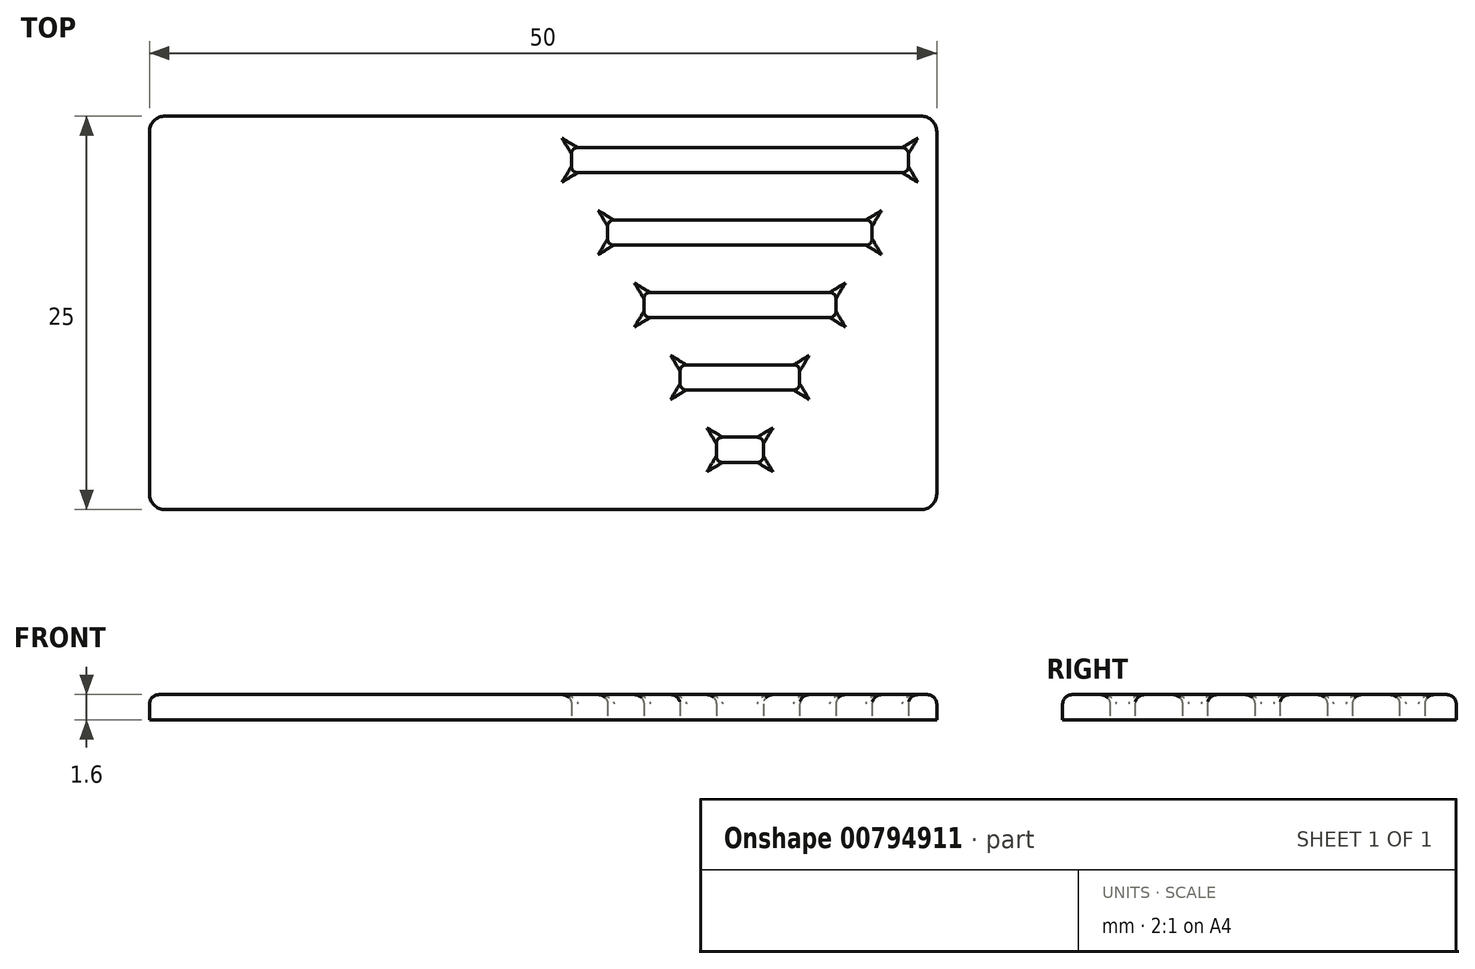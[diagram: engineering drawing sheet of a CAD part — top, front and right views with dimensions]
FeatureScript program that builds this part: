
annotation { "Feature Type Name" : "Feature", "Feature Type Description" : "" }
export const myFeature = defineFeature(function(context is Context, id is Id, definition is map)
    precondition{}
    {
        {
            var Q0;
            Q0=qCreatedBy(makeId("Top.planeOp"),FACE);
            var sketch = newSketch(context, id + "F0", { "sketchPlane" : qUnion([Q0])});
            skLineSegment(sketch, "E0.bottom", {"start": v(-25, 12.5) * mm, "end": v(25, 12.5) * mm});
            skLineSegment(sketch, "E0.top", {"start": v(-25, -12.5) * mm, "end": v(25, -12.5) * mm});
            skLineSegment(sketch, "E0.left", {"start": v(-25, 12.5) * mm, "end": v(-25, -12.5) * mm});
            skLineSegment(sketch, "E0.right", {"start": v(25, 12.5) * mm, "end": v(25, -12.5) * mm});
            skLineSegment(sketch, "E1", {"start": v(-25, 12.5) * mm, "end": v(25, -12.5) * mm, "construction": true});
            skLineSegment(sketch, "E2", {"start": v(0, 12.5) * mm, "end": v(0, -12.5) * mm, "construction": true});
            skLineSegment(sketch, "E3", {"start": v(0, 12.5) * mm, "end": v(12.5, -12.5) * mm, "construction": true});
            skLineSegment(sketch, "E4", {"start": v(12.5, -12.5) * mm, "end": v(25, 12.5) * mm, "construction": true});
            skLineSegment(sketch, "E5.bottom", {"start": v(11, -9.5) * mm, "end": v(14, -9.5) * mm});
            skLineSegment(sketch, "E5.top", {"start": v(11, -7.9) * mm, "end": v(14, -7.9) * mm});
            skLineSegment(sketch, "E5.left", {"start": v(11, -9.5) * mm, "end": v(11, -7.9) * mm});
            skLineSegment(sketch, "E5.right", {"start": v(14, -9.5) * mm, "end": v(14, -7.9) * mm});
            skLineSegment(sketch, "E6.bottom", {"start": v(6.4, -0.3) * mm, "end": v(18.6, -0.3) * mm});
            skLineSegment(sketch, "E6.top", {"start": v(6.4, 1.3) * mm, "end": v(18.6, 1.3) * mm});
            skLineSegment(sketch, "E6.left", {"start": v(6.4, -0.3) * mm, "end": v(6.4, 1.3) * mm});
            skLineSegment(sketch, "E6.right", {"start": v(18.6, -0.3) * mm, "end": v(18.6, 1.3) * mm});
            skLineSegment(sketch, "E7.bottom", {"start": v(8.7, -4.9) * mm, "end": v(16.3, -4.9) * mm});
            skLineSegment(sketch, "E7.top", {"start": v(8.7, -3.3) * mm, "end": v(16.3, -3.3) * mm});
            skLineSegment(sketch, "E7.left", {"start": v(8.7, -4.9) * mm, "end": v(8.7, -3.3) * mm});
            skLineSegment(sketch, "E7.right", {"start": v(16.3, -4.9) * mm, "end": v(16.3, -3.3) * mm});
            skLineSegment(sketch, "E8", {"start": v(11, -12.5) * mm, "end": v(11, -9.5) * mm, "construction": true});
            skLineSegment(sketch, "E9", {"start": v(11, -7.9) * mm, "end": v(11, -4.9) * mm, "construction": true});
            skLineSegment(sketch, "E10", {"start": v(8.7, -3.3) * mm, "end": v(8.7, -0.3) * mm, "construction": true});
            skLineSegment(sketch, "E11.bottom", {"start": v(4.1, 4.3) * mm, "end": v(20.9, 4.3) * mm});
            skLineSegment(sketch, "E11.top", {"start": v(4.1, 5.9) * mm, "end": v(20.9, 5.9) * mm});
            skLineSegment(sketch, "E11.left", {"start": v(4.1, 4.3) * mm, "end": v(4.1, 5.9) * mm});
            skLineSegment(sketch, "E11.right", {"start": v(20.9, 4.3) * mm, "end": v(20.9, 5.9) * mm});
            skLineSegment(sketch, "E12", {"start": v(6.4, 1.3) * mm, "end": v(6.4, 4.3) * mm, "construction": true});
            skLineSegment(sketch, "E13.bottom", {"start": v(1.8, 8.9) * mm, "end": v(23.2, 8.9) * mm});
            skLineSegment(sketch, "E13.top", {"start": v(1.8, 10.5) * mm, "end": v(23.2, 10.5) * mm});
            skLineSegment(sketch, "E13.left", {"start": v(1.8, 8.9) * mm, "end": v(1.8, 10.5) * mm});
            skLineSegment(sketch, "E13.right", {"start": v(23.2, 8.9) * mm, "end": v(23.2, 10.5) * mm});
            skLineSegment(sketch, "E14", {"start": v(4.1, 5.9) * mm, "end": v(4.1, 8.9) * mm, "construction": true});
            skLineSegment(sketch, "E15", {"start": v(4.1, 10.5) * mm, "end": v(4.1, 12.5) * mm, "construction": true});
            skSolve(sketch);
        }
        {
            var Q0;
            Q0=makeQuery(id+"F0.imprint","IMPRINT",FACE,{"disambiguationData":[TD([[makeQuery(id+"F0.imprint","IMPRINT",EDGE,{"derivedFrom":sQuery(id+"F0.wireOp",EDGE,"E0.bottom")}),-1.0]])]});
            extrude(context, id + "F1", {"entities" : qUnion([Q0]), "depth" : 1.6 * mm, "offsetDistance" : 25 * mm});
        }
        {
            var Q0;
            Q0=makeQuery(id+"F1.opExtrude","CAP_FACE",FACE,{"disambiguationData":[OSD([sQuery(id+"F0.wireOp",EDGE,"E0.bottom"),sQuery(id+"F0.wireOp",EDGE,"E0.top"),sQuery(id+"F0.wireOp",EDGE,"E0.left"),sQuery(id+"F0.wireOp",EDGE,"E0.right"),sQuery(id+"F0.wireOp",EDGE,"E5.bottom"),sQuery(id+"F0.wireOp",EDGE,"E5.top"),sQuery(id+"F0.wireOp",EDGE,"E5.left"),sQuery(id+"F0.wireOp",EDGE,"E5.right"),sQuery(id+"F0.wireOp",EDGE,"E6.bottom"),sQuery(id+"F0.wireOp",EDGE,"E6.top"),sQuery(id+"F0.wireOp",EDGE,"E6.left"),sQuery(id+"F0.wireOp",EDGE,"E6.right"),sQuery(id+"F0.wireOp",EDGE,"E7.bottom"),sQuery(id+"F0.wireOp",EDGE,"E7.top"),sQuery(id+"F0.wireOp",EDGE,"E7.left"),sQuery(id+"F0.wireOp",EDGE,"E7.right"),sQuery(id+"F0.wireOp",EDGE,"E11.bottom"),sQuery(id+"F0.wireOp",EDGE,"E11.top"),sQuery(id+"F0.wireOp",EDGE,"E11.left"),sQuery(id+"F0.wireOp",EDGE,"E11.right"),sQuery(id+"F0.wireOp",EDGE,"E13.bottom"),sQuery(id+"F0.wireOp",EDGE,"E13.top"),sQuery(id+"F0.wireOp",EDGE,"E13.left"),sQuery(id+"F0.wireOp",EDGE,"E13.right")])],"isStart":false});
            fillet(context, id + "F2", {"entities" : qUnion([Q0]), "radius" : 0.6 * mm, "tangentPropagation" : true, "allowEdgeOverflow" : false});
        }
        {
            var Q0;
            Q0=makeQuery(id+"F1.opExtrude","SWEPT_EDGE",EDGE,{"disambiguationData":[OSD([sQuery(id+"F0.wireOp",EDGE,"E11.bottom"),sQuery(id+"F0.wireOp",EDGE,"E11.right")])]});
            var Q1;
            Q1=makeQuery(id+"F1.opExtrude","SWEPT_EDGE",EDGE,{"disambiguationData":[OSD([sQuery(id+"F0.wireOp",EDGE,"E6.bottom"),sQuery(id+"F0.wireOp",EDGE,"E6.right")])]});
            var Q2;
            Q2=makeQuery(id+"F1.opExtrude","SWEPT_EDGE",EDGE,{"disambiguationData":[OSD([sQuery(id+"F0.wireOp",EDGE,"E7.bottom"),sQuery(id+"F0.wireOp",EDGE,"E7.right")])]});
            var Q3;
            Q3=makeQuery(id+"F1.opExtrude","SWEPT_EDGE",EDGE,{"disambiguationData":[OSD([sQuery(id+"F0.wireOp",EDGE,"E5.bottom"),sQuery(id+"F0.wireOp",EDGE,"E5.right")])]});
            var Q4;
            Q4=makeQuery(id+"F1.opExtrude","SWEPT_EDGE",EDGE,{"disambiguationData":[OSD([sQuery(id+"F0.wireOp",EDGE,"E7.top"),sQuery(id+"F0.wireOp",EDGE,"E7.right")])]});
            var Q5;
            Q5=makeQuery(id+"F1.opExtrude","SWEPT_EDGE",EDGE,{"disambiguationData":[OSD([sQuery(id+"F0.wireOp",EDGE,"E6.top"),sQuery(id+"F0.wireOp",EDGE,"E6.right")])]});
            var Q6;
            Q6=makeQuery(id+"F1.opExtrude","SWEPT_EDGE",EDGE,{"disambiguationData":[OSD([sQuery(id+"F0.wireOp",EDGE,"E11.top"),sQuery(id+"F0.wireOp",EDGE,"E11.right")])]});
            var Q7;
            Q7=makeQuery(id+"F1.opExtrude","SWEPT_EDGE",EDGE,{"disambiguationData":[OSD([sQuery(id+"F0.wireOp",EDGE,"E13.top"),sQuery(id+"F0.wireOp",EDGE,"E13.right")])]});
            var Q8;
            Q8=makeQuery(id+"F1.opExtrude","SWEPT_EDGE",EDGE,{"disambiguationData":[OSD([sQuery(id+"F0.wireOp",EDGE,"E5.top"),sQuery(id+"F0.wireOp",EDGE,"E5.right")])]});
            var Q9;
            Q9=makeQuery(id+"F1.opExtrude","SWEPT_EDGE",EDGE,{"disambiguationData":[OSD([sQuery(id+"F0.wireOp",EDGE,"E13.top"),sQuery(id+"F0.wireOp",EDGE,"E13.left")])]});
            var Q10;
            Q10=makeQuery(id+"F1.opExtrude","SWEPT_EDGE",EDGE,{"disambiguationData":[OSD([sQuery(id+"F0.wireOp",EDGE,"E11.top"),sQuery(id+"F0.wireOp",EDGE,"E11.left")])]});
            var Q11;
            Q11=makeQuery(id+"F1.opExtrude","SWEPT_EDGE",EDGE,{"disambiguationData":[OSD([sQuery(id+"F0.wireOp",EDGE,"E6.top"),sQuery(id+"F0.wireOp",EDGE,"E6.left")])]});
            var Q12;
            Q12=makeQuery(id+"F1.opExtrude","SWEPT_EDGE",EDGE,{"disambiguationData":[OSD([sQuery(id+"F0.wireOp",EDGE,"E7.top"),sQuery(id+"F0.wireOp",EDGE,"E7.left")])]});
            var Q13;
            Q13=makeQuery(id+"F1.opExtrude","SWEPT_EDGE",EDGE,{"disambiguationData":[OSD([sQuery(id+"F0.wireOp",EDGE,"E5.top"),sQuery(id+"F0.wireOp",EDGE,"E5.left")])]});
            var Q14;
            Q14=makeQuery(id+"F1.opExtrude","SWEPT_EDGE",EDGE,{"disambiguationData":[OSD([sQuery(id+"F0.wireOp",EDGE,"E7.bottom"),sQuery(id+"F0.wireOp",EDGE,"E7.left")])]});
            var Q15;
            Q15=makeQuery(id+"F1.opExtrude","SWEPT_EDGE",EDGE,{"disambiguationData":[OSD([sQuery(id+"F0.wireOp",EDGE,"E6.bottom"),sQuery(id+"F0.wireOp",EDGE,"E6.left")])]});
            var Q16;
            Q16=makeQuery(id+"F1.opExtrude","SWEPT_EDGE",EDGE,{"disambiguationData":[OSD([sQuery(id+"F0.wireOp",EDGE,"E11.bottom"),sQuery(id+"F0.wireOp",EDGE,"E11.left")])]});
            var Q17;
            Q17=makeQuery(id+"F1.opExtrude","SWEPT_EDGE",EDGE,{"disambiguationData":[OSD([sQuery(id+"F0.wireOp",EDGE,"E13.bottom"),sQuery(id+"F0.wireOp",EDGE,"E13.left")])]});
            var Q18;
            Q18=makeQuery(id+"F1.opExtrude","SWEPT_EDGE",EDGE,{"disambiguationData":[OSD([sQuery(id+"F0.wireOp",EDGE,"E5.bottom"),sQuery(id+"F0.wireOp",EDGE,"E5.left")])]});
            var Q19;
            Q19=makeQuery(id+"F1.opExtrude","SWEPT_EDGE",EDGE,{"disambiguationData":[OSD([sQuery(id+"F0.wireOp",EDGE,"E13.bottom"),sQuery(id+"F0.wireOp",EDGE,"E13.right")])]});
            fillet(context, id + "F3", {"entities" : qUnion([Q0, Q1, Q2, Q3, Q4, Q5, Q6, Q7, Q8, Q9, Q10, Q11, Q12, Q13, Q14, Q15, Q16, Q17, Q18, Q19]), "radius" : 0.4 * mm, "tangentPropagation" : true, "allowEdgeOverflow" : false});
        }
        {
            var Q0;
            Q0=makeQuery(id+"F1.opExtrude","SWEPT_EDGE",EDGE,{"disambiguationData":[OSD([sQuery(id+"F0.wireOp",EDGE,"E0.bottom"),sQuery(id+"F0.wireOp",EDGE,"E0.right")])]});
            var Q1;
            Q1=makeQuery(id+"F1.opExtrude","SWEPT_EDGE",EDGE,{"disambiguationData":[OSD([sQuery(id+"F0.wireOp",EDGE,"E0.top"),sQuery(id+"F0.wireOp",EDGE,"E0.right")])]});
            var Q2;
            Q2=makeQuery(id+"F1.opExtrude","SWEPT_EDGE",EDGE,{"disambiguationData":[OSD([sQuery(id+"F0.wireOp",EDGE,"E0.top"),sQuery(id+"F0.wireOp",EDGE,"E0.left")])]});
            var Q3;
            Q3=makeQuery(id+"F1.opExtrude","SWEPT_EDGE",EDGE,{"disambiguationData":[OSD([sQuery(id+"F0.wireOp",EDGE,"E0.bottom"),sQuery(id+"F0.wireOp",EDGE,"E0.left")])]});
            fillet(context, id + "F4", {"entities" : qUnion([Q0, Q1, Q2, Q3]), "radius" : 1 * mm, "tangentPropagation" : true, "allowEdgeOverflow" : false});
        }
    });
